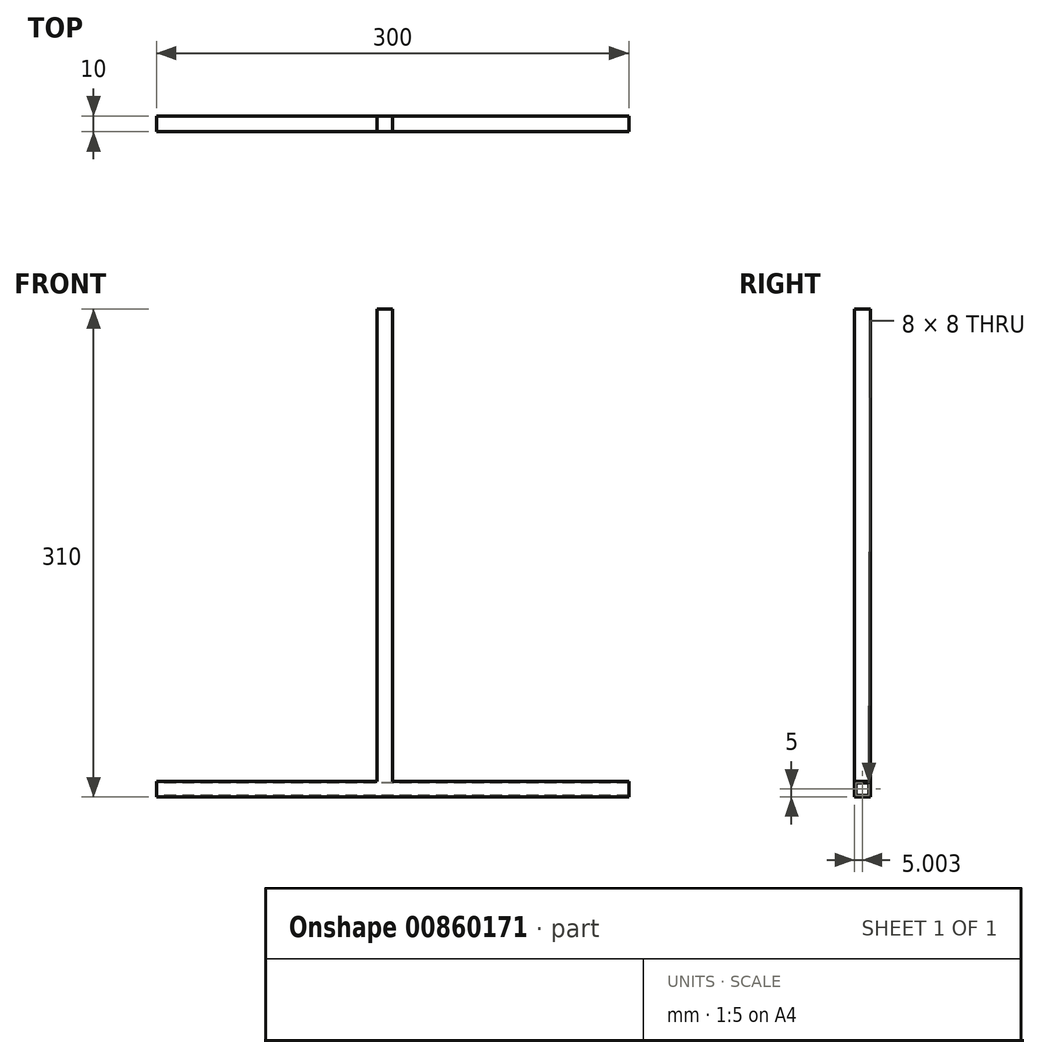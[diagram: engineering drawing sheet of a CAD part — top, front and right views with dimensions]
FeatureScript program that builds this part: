
annotation { "Feature Type Name" : "Feature", "Feature Type Description" : "" }
export const myFeature = defineFeature(function(context is Context, id is Id, definition is map)
    precondition{}
    {
        {
            var Q0;
            Q0=qCreatedBy(makeId("Right.planeOp"),FACE);
            var sketch = newSketch(context, id + "F0", { "sketchPlane" : qUnion([Q0])});
            skLineSegment(sketch, "E0.bottom", {"start": v(37.82, 1) * mm, "end": v(27.82, 1) * mm});
            skLineSegment(sketch, "E0.top", {"start": v(37.82, -9) * mm, "end": v(27.82, -9) * mm});
            skLineSegment(sketch, "E0.left", {"start": v(37.82, 1) * mm, "end": v(37.82, -9) * mm});
            skLineSegment(sketch, "E0.right", {"start": v(27.82, 1) * mm, "end": v(27.82, -9) * mm});
            skLineSegment(sketch, "E1.bottom", {"start": v(36.82, 0) * mm, "end": v(28.82, 0) * mm});
            skLineSegment(sketch, "E1.top", {"start": v(36.82, -8) * mm, "end": v(28.82, -8) * mm});
            skLineSegment(sketch, "E1.left", {"start": v(36.82, 0) * mm, "end": v(36.82, -8) * mm});
            skLineSegment(sketch, "E1.right", {"start": v(28.82, 0) * mm, "end": v(28.82, -8) * mm});
            skSolve(sketch);
        }
        {
            var Q0;
            Q0=makeQuery(id+"F0.imprint","IMPRINT",FACE,{"disambiguationData":[TD([[makeQuery(id+"F0.imprint","IMPRINT",EDGE,{"derivedFrom":sQuery(id+"F0.wireOp",EDGE,"E0.bottom")}),1.0]])]});
            extrude(context, id + "F1", {"entities" : qUnion([Q0]), "depth" : 300 * mm, "offsetDistance" : 25 * mm});
        }
        {
            var Q0;
            Q0=makeQuery(id+"F1.opExtrude","SWEPT_FACE",FACE,{"disambiguationData":[OSD([sQuery(id+"F0.wireOp",EDGE,"E0.bottom")])]});
            var sketch = newSketch(context, id + "F2", { "sketchPlane" : qUnion([Q0])});
            skLineSegment(sketch, "E2.bottom", {"start": v(140, 37.82) * mm, "end": v(150, 37.82) * mm});
            skLineSegment(sketch, "E2.top", {"start": v(140, 27.82) * mm, "end": v(150, 27.82) * mm});
            skLineSegment(sketch, "E2.left", {"start": v(140, 37.82) * mm, "end": v(140, 27.82) * mm});
            skLineSegment(sketch, "E2.right", {"start": v(150, 37.82) * mm, "end": v(150, 27.82) * mm});
            skSolve(sketch);
        }
        {
            var Q0;
            Q0 = qSketchRegion(id + "F2", true);
            extrude(context, id + "F3", {"entities" : qUnion([Q0]), "operationType" : NewBodyOperationType.ADD, "depth" : 300 * mm, "offsetDistance" : 25 * mm});
        }
    });
